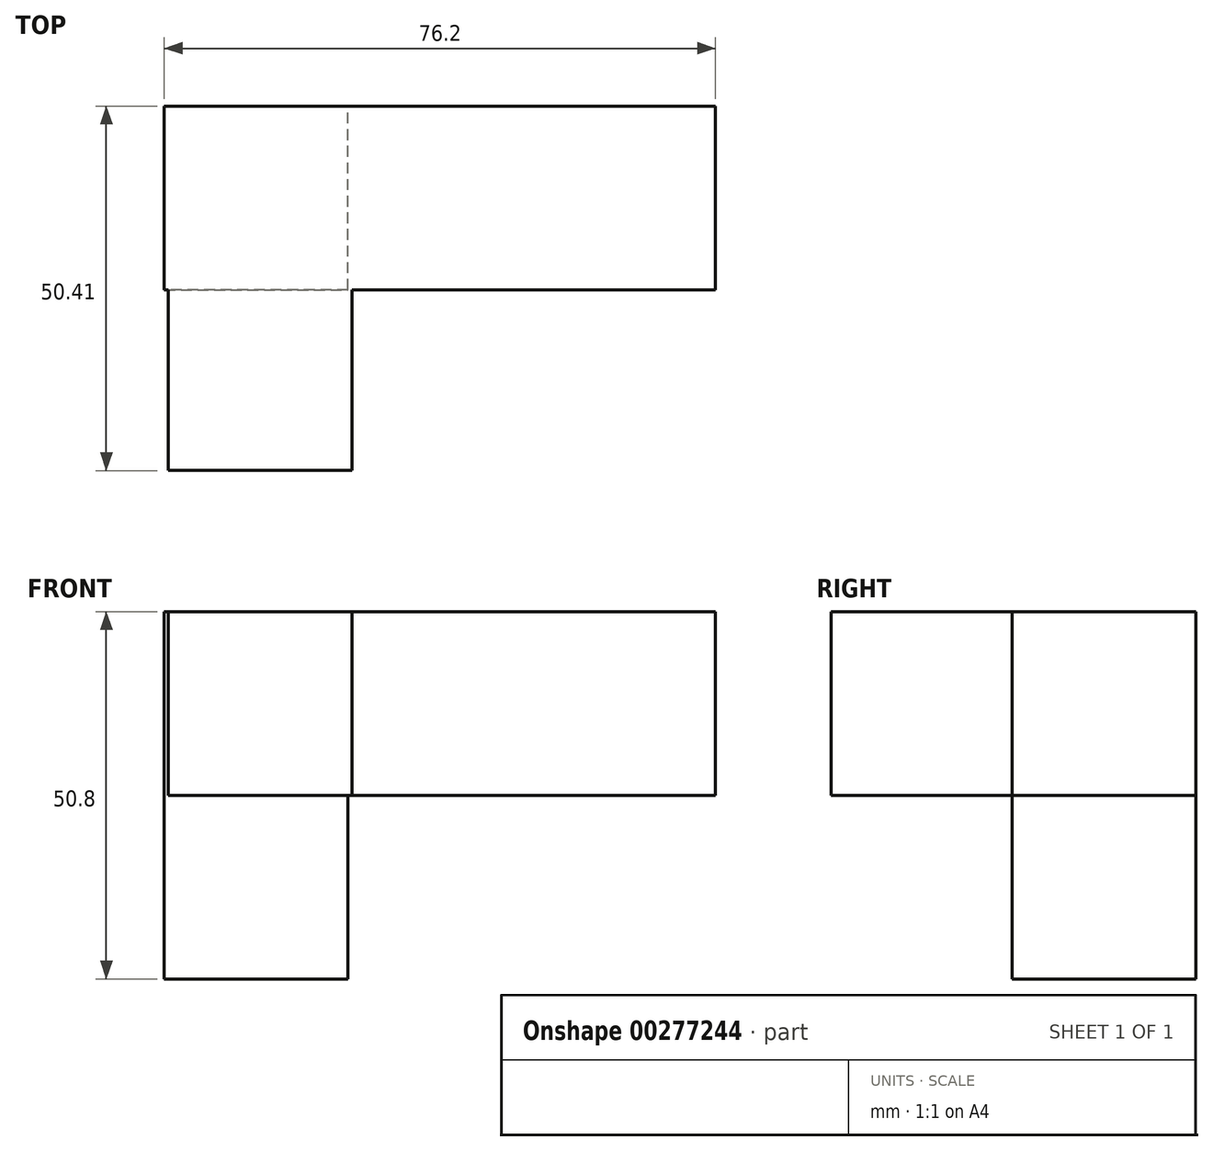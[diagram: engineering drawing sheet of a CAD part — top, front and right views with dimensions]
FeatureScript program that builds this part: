
annotation { "Feature Type Name" : "Feature", "Feature Type Description" : "" }
export const myFeature = defineFeature(function(context is Context, id is Id, definition is map)
    precondition{}
    {
        {
            var Q0;
            Q0=qCreatedBy(makeId("Front.planeOp"),FACE);
            var sketch = newSketch(context, id + "F0", { "sketchPlane" : qUnion([Q0])});
            skLineSegment(sketch, "E0", {"start": v(-50.8, 0) * mm, "end": v(25.4, 0) * mm});
            skLineSegment(sketch, "E1", {"start": v(25.4, 0) * mm, "end": v(25.4, 25.4) * mm});
            skLineSegment(sketch, "E2", {"start": v(25.4, 25.4) * mm, "end": v(0, 25.4) * mm});
            skLineSegment(sketch, "E3", {"start": v(0, 25.4) * mm, "end": v(0, 0) * mm});
            skLineSegment(sketch, "E4", {"start": v(0, 0) * mm, "end": v(0, 25.4) * mm});
            skLineSegment(sketch, "E5", {"start": v(0, 25.4) * mm, "end": v(-25.4, 25.4) * mm});
            skLineSegment(sketch, "E6", {"start": v(-25.4, 25.4) * mm, "end": v(-25.4, 0) * mm});
            skLineSegment(sketch, "E7", {"start": v(-25.4, 0) * mm, "end": v(0, 0) * mm});
            skLineSegment(sketch, "E8", {"start": v(-25.4, 25.4) * mm, "end": v(-50.8, 25.4) * mm});
            skLineSegment(sketch, "E9", {"start": v(-50.8, 25.4) * mm, "end": v(-50.8, 0) * mm});
            skLineSegment(sketch, "E10", {"start": v(-25.4, 0) * mm, "end": v(-25.4, 25.4) * mm});
            skLineSegment(sketch, "E11", {"start": v(-50.8, 0) * mm, "end": v(-50.8, -25.4) * mm});
            skLineSegment(sketch, "E12", {"start": v(-50.8, -25.4) * mm, "end": v(-25.4, -25.4) * mm});
            skLineSegment(sketch, "E13", {"start": v(-25.4, -25.4) * mm, "end": v(-25.4, 0) * mm});
            skSolve(sketch);
        }
        {
            var Q0;
            Q0 = qSketchRegion(id + "F0", true);
            extrude(context, id + "F1", {"entities" : qUnion([Q0]), "depth" : 25.4 * mm});
        }
        {
            var Q0;
            Q0=qCreatedBy(makeId("Top.planeOp"),FACE);
            var sketch = newSketch(context, id + "F2", { "sketchPlane" : qUnion([Q0])});
            skLineSegment(sketch, "E14", {"start": v(-24.85, -25) * mm, "end": v(-24.85, -50.4) * mm});
            skLineSegment(sketch, "E15", {"start": v(-24.85, -50.4) * mm, "end": v(-50.25, -50.4) * mm});
            skLineSegment(sketch, "E16", {"start": v(-50.25, -50.4) * mm, "end": v(-50.25, -25) * mm});
            skLineSegment(sketch, "E17", {"start": v(-50.25, -25) * mm, "end": v(-24.85, -25) * mm});
            skSolve(sketch);
        }
        {
            var Q0;
            Q0 = qSketchRegion(id + "F2", true);
            extrude(context, id + "F3", {"entities" : qUnion([Q0]), "operationType" : NewBodyOperationType.ADD, "depth" : 25.4 * mm});
        }
    });
